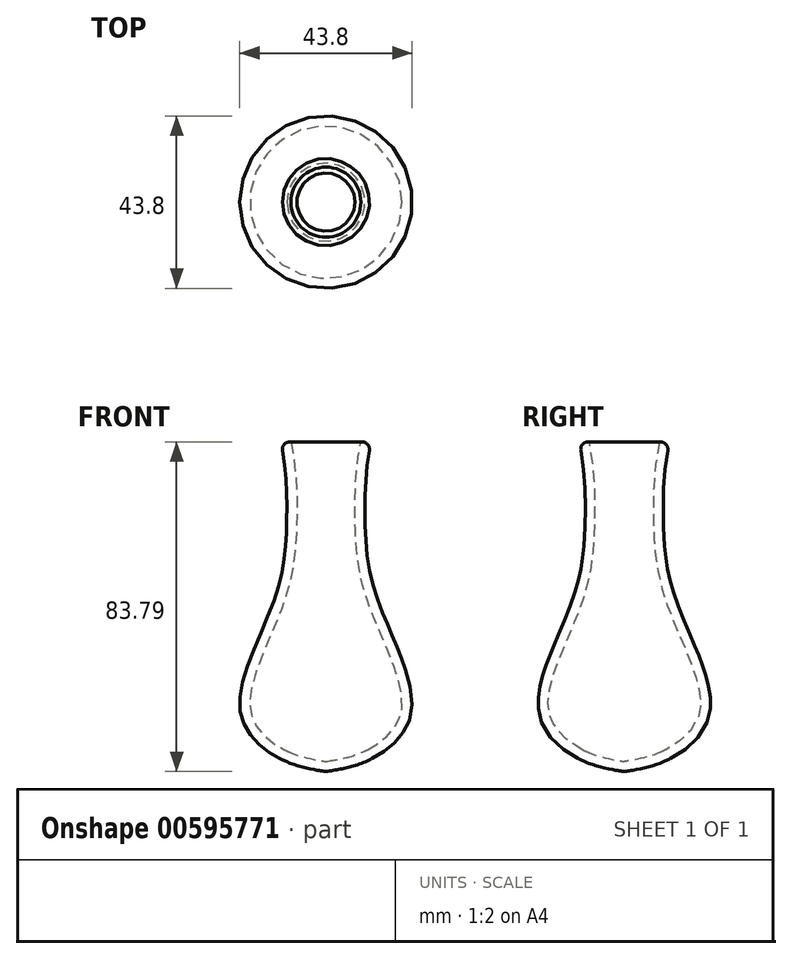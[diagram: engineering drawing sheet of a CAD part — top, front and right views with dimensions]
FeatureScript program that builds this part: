
annotation { "Feature Type Name" : "Feature", "Feature Type Description" : "" }
export const myFeature = defineFeature(function(context is Context, id is Id, definition is map)
    precondition{}
    {
        {
            var Q0;
            Q0=qCreatedBy(makeId("Front.planeOp"),FACE);
            var sketch = newSketch(context, id + "F0", { "sketchPlane" : qUnion([Q0])});
            skFitSpline(sketch, "E0", {"points": [v(0, 0) * mm, v(11.01, 2.96) * mm, v(21.75, 15.23) * mm, v(13.26, 43.3) * mm, v(9.96, 63.34) * mm, v(11.61, 84.32) * mm], "startDerivative": vector(68.77, 10.87) * mm, "endDerivative": vector(24.05, 102.1) * mm});
            skArc(sketch, "E1", {"start": v(0, 82.85) * mm, "mid": v(5.84, 83.3) * mm, "end": v(11.61, 84.32) * mm});
            skLineSegment(sketch, "E2", {"start": v(0, 0) * mm, "end": v(0, 86.69) * mm});
            skLineSegment(sketch, "E3", {"start": v(0, 0) * mm, "end": v(5.29, 0) * mm});
            skFitSpline(sketch, "E4", {"points": [v(7.72, 0) * mm, v(11.01, 2.96) * mm], "startDerivative": vector(3.19, 2.97) * mm, "endDerivative": vector(3.19, 2.97) * mm});
            skArc(sketch, "E5.filletArc", {"start": v(5.29, 0) * mm, "mid": v(7.54, 0.41) * mm, "end": v(9.5, 1.6) * mm});
            skArc(sketch, "E6.filletArc", {"start": v(11.73, 3.32) * mm, "mid": v(11.03, 2.9) * mm, "end": v(10.39, 2.39) * mm});
            skSolve(sketch);
        }
        {
            var Q0;
            Q0=makeQuery(id+"F0.imprint","IMPRINT",FACE,{"disambiguationData":[TD([[makeQuery(id+"F0.imprint","IMPRINT",EDGE,{"derivedFrom":sQuery(id+"F0.wireOp",EDGE,"E0")}),1.0]])]});
            var Q1;
            Q1=sQuery(id+"F0.wireOp",EDGE,"E2");
            revolve(context, id + "F1", {"entities" : qUnion([Q0]), "axis" : qUnion([Q1]), "revolveType" : RevolveType.FULL});
        }
        {
            var Q0;
            Q0=makeQuery(id+"F1.opRevolve","SWEPT_FACE",FACE,{"disambiguationData":[OSD([sQuery(id+"F0.wireOp",EDGE,"E1")])]});
            shell(context, id + "F2", {"entities" : qUnion([Q0]), "thickness" : 2.54 * mm});
        }
        {
            var Q0;
            Q0=makeQuery(id+"F1.opRevolve","SWEPT_EDGE",EDGE,{"disambiguationData":[OSD([sQuery(id+"F0.wireOp",EDGE,"E0"),sQuery(id+"F0.wireOp",EDGE,"E1")])]});
            fillet(context, id + "F3", {"entities" : qUnion([Q0]), "radius" : 1.9 * mm, "tangentPropagation" : true, "allowEdgeOverflow" : false});
        }
    });
